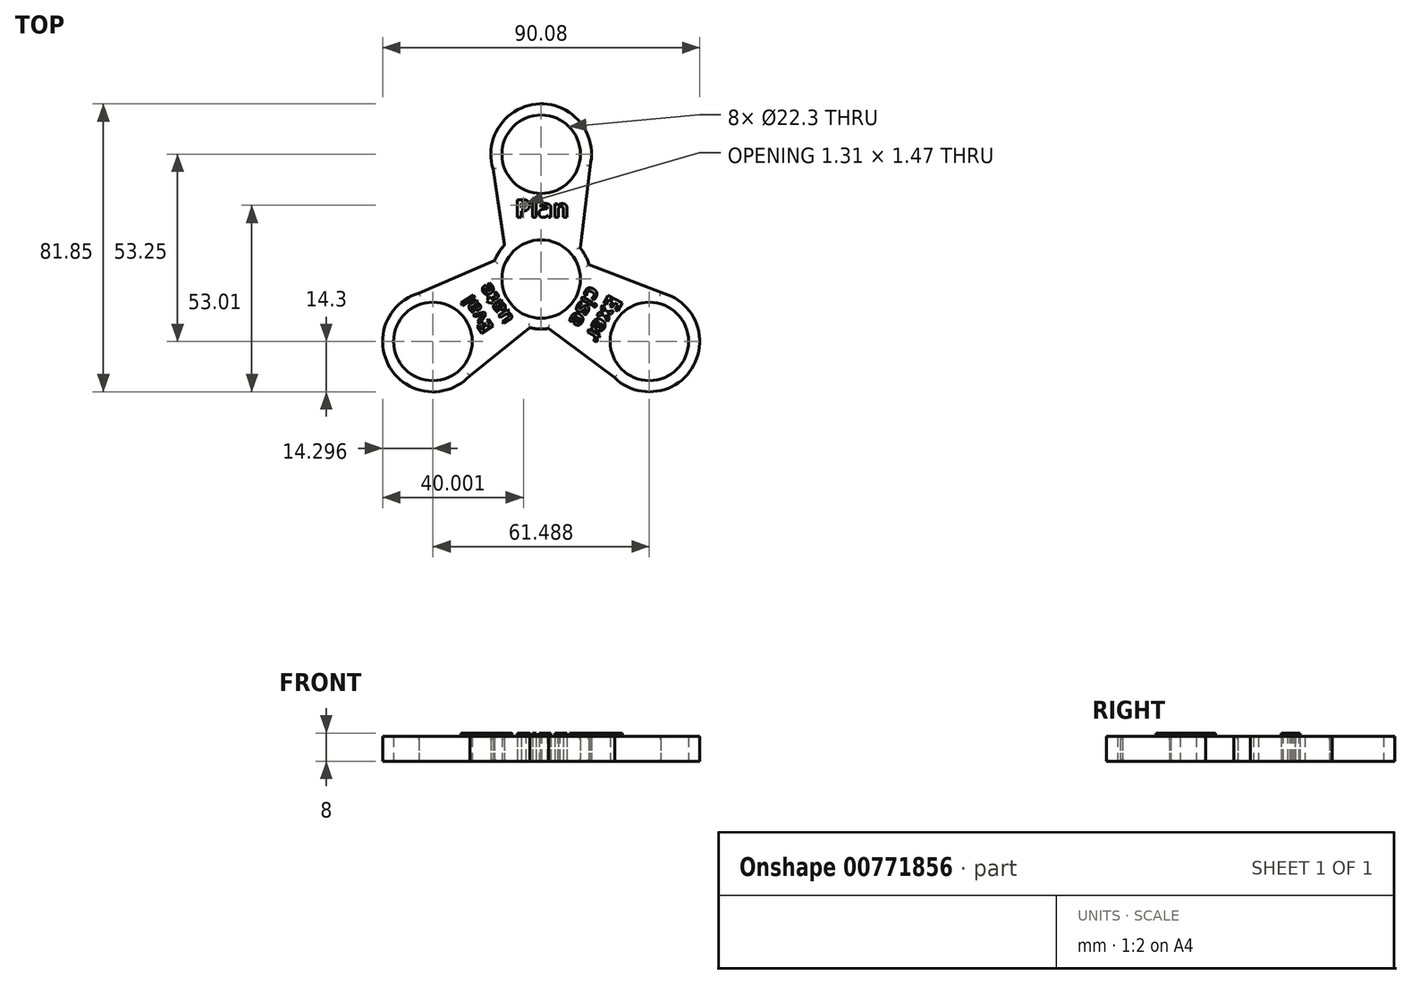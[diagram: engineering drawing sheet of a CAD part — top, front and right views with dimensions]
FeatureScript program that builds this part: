
annotation { "Feature Type Name" : "Feature", "Feature Type Description" : "" }
export const myFeature = defineFeature(function(context is Context, id is Id, definition is map)
    precondition{}
    {
        {
            var Q0;
            Q0=qCreatedBy(makeId("Top.planeOp"),FACE);
            var sketch = newSketch(context, id + "F0", { "sketchPlane" : qUnion([Q0])});
            skCircle(sketch, "E0", {"center": v(0, 0) * mm, "radius": 11.15 * mm});
            skArc(sketch, "E1", {"start": v(-3.17, -13.84) * mm, "mid": v(-0.55, -14.19) * mm, "end": v(2.09, -14.05) * mm});
            skArc(sketch, "E2", {"start": v(13.89, 32.1) * mm, "mid": v(-0.4, 49.8) * mm, "end": v(-13.67, 31.31) * mm});
            skCircle(sketch, "E3", {"center": v(0, 35.5) * mm, "radius": 11.15 * mm});
            skLineSegment(sketch, "E4", {"start": v(13.89, 32.1) * mm, "end": v(11.12, 8.83) * mm});
            skLineSegment(sketch, "E5", {"start": v(-13.67, 31.31) * mm, "end": v(-10.4, 9.66) * mm});
            skArc(sketch, "E6.1.0", {"start": v(-34.74, -4.02) * mm, "mid": v(-42.92, -25.25) * mm, "end": v(-20.28, -27.5) * mm});
            skLineSegment(sketch, "E6.1.1", {"start": v(-20.28, -27.5) * mm, "end": v(-3.17, -13.84) * mm});
            skLineSegment(sketch, "E6.1.2", {"start": v(-34.74, -4.02) * mm, "end": v(-13.2, 5.22) * mm});
            skCircle(sketch, "E6.1.3", {"center": v(-30.74, -17.75) * mm, "radius": 11.15 * mm});
            skArc(sketch, "E6.2.0", {"start": v(20.85, -28.08) * mm, "mid": v(43.33, -24.55) * mm, "end": v(33.95, -3.82) * mm});
            skLineSegment(sketch, "E6.2.1", {"start": v(33.95, -3.82) * mm, "end": v(13.57, 4.18) * mm});
            skLineSegment(sketch, "E6.2.2", {"start": v(20.85, -28.08) * mm, "end": v(2.09, -14.05) * mm});
            skCircle(sketch, "E6.2.3", {"center": v(30.74, -17.75) * mm, "radius": 11.15 * mm});
            skPoint(sketch, "E7.orphan", {"position": v(14.3, 35.55) * mm});
            skPoint(sketch, "E8.orphan", {"position": v(-14.3, 35.46) * mm});
            skPoint(sketch, "E9.orphan", {"position": v(-37.94, -5.4) * mm});
            skPoint(sketch, "E10.orphan", {"position": v(-23.56, -30.12) * mm});
            skArc(sketch, "E11.trimOffspring", {"start": v(13.57, 4.18) * mm, "mid": v(12.56, 6.62) * mm, "end": v(11.12, 8.83) * mm});
            skPoint(sketch, "E12.orphan", {"position": v(23.64, -30.16) * mm});
            skPoint(sketch, "E13.orphan", {"position": v(37.86, -5.35) * mm});
            skArc(sketch, "E14.trimOffspring", {"start": v(-10.4, 9.66) * mm, "mid": v(-12.01, 7.57) * mm, "end": v(-13.2, 5.22) * mm});
            skPoint(sketch, "E15.firstSnap0", {"position": v(-12.04, 20.49) * mm});
            skSolve(sketch);
        }
        {
            var Q0;
            Q0 = qSketchRegion(id + "F0", true);
            extrude(context, id + "F1", {"entities" : qUnion([Q0]), "depth" : 7 * mm, "offsetDistance" : 25 * mm});
        }
        {
            var Q0;
            Q0=makeQuery(id+"F1.opExtrude","CAP_EDGE",EDGE,{"disambiguationData":[OSD([sQuery(id+"F0.wireOp",EDGE,"E2")])],"isStart":false});
            var Q1;
            Q1=makeQuery(id+"F1.opExtrude","CAP_EDGE",EDGE,{"disambiguationData":[OSD([sQuery(id+"F0.wireOp",EDGE,"E2")])],"isStart":true});
            var Q2;
            Q2=makeQuery(id+"F1.opExtrude","SWEPT_EDGE",EDGE,{"disambiguationData":[OSD([sQuery(id+"F0.wireOp",EDGE,"E5"),sQuery(id+"F0.wireOp",EDGE,"E14.trimOffspring")])]});
            var Q3;
            Q3=makeQuery(id+"F1.opExtrude","CAP_EDGE",EDGE,{"disambiguationData":[OSD([sQuery(id+"F0.wireOp",EDGE,"E5")])],"isStart":false});
            var Q4;
            Q4=makeQuery(id+"F1.opExtrude","CAP_EDGE",EDGE,{"disambiguationData":[OSD([sQuery(id+"F0.wireOp",EDGE,"E5")])],"isStart":true});
            var Q5;
            Q5=makeQuery(id+"F1.opExtrude","CAP_EDGE",EDGE,{"disambiguationData":[OSD([sQuery(id+"F0.wireOp",EDGE,"E6.1.2")])],"isStart":true});
            var Q6;
            Q6=makeQuery(id+"F1.opExtrude","CAP_EDGE",EDGE,{"disambiguationData":[OSD([sQuery(id+"F0.wireOp",EDGE,"E14.trimOffspring")])],"isStart":true});
            var Q7;
            Q7=makeQuery(id+"F1.opExtrude","CAP_EDGE",EDGE,{"disambiguationData":[OSD([sQuery(id+"F0.wireOp",EDGE,"E14.trimOffspring")])],"isStart":false});
            var Q8;
            Q8=makeQuery(id+"F1.opExtrude","CAP_EDGE",EDGE,{"disambiguationData":[OSD([sQuery(id+"F0.wireOp",EDGE,"E6.1.2")])],"isStart":false});
            var Q9;
            Q9=makeQuery(id+"F1.opExtrude","CAP_EDGE",EDGE,{"disambiguationData":[OSD([sQuery(id+"F0.wireOp",EDGE,"E6.1.0")])],"isStart":true});
            var Q10;
            Q10=makeQuery(id+"F1.opExtrude","CAP_EDGE",EDGE,{"disambiguationData":[OSD([sQuery(id+"F0.wireOp",EDGE,"E6.1.0")])],"isStart":false});
            var Q11;
            Q11=makeQuery(id+"F1.opExtrude","CAP_EDGE",EDGE,{"disambiguationData":[OSD([sQuery(id+"F0.wireOp",EDGE,"E6.1.1")])],"isStart":true});
            var Q12;
            Q12=makeQuery(id+"F1.opExtrude","CAP_EDGE",EDGE,{"disambiguationData":[OSD([sQuery(id+"F0.wireOp",EDGE,"E6.1.1")])],"isStart":false});
            var Q13;
            Q13=makeQuery(id+"F1.opExtrude","CAP_EDGE",EDGE,{"disambiguationData":[OSD([sQuery(id+"F0.wireOp",EDGE,"E1")])],"isStart":false});
            var Q14;
            Q14=makeQuery(id+"F1.opExtrude","CAP_EDGE",EDGE,{"disambiguationData":[OSD([sQuery(id+"F0.wireOp",EDGE,"E1")])],"isStart":true});
            var Q15;
            Q15=makeQuery(id+"F1.opExtrude","CAP_EDGE",EDGE,{"disambiguationData":[OSD([sQuery(id+"F0.wireOp",EDGE,"E6.2.2")])],"isStart":false});
            var Q16;
            Q16=makeQuery(id+"F1.opExtrude","CAP_EDGE",EDGE,{"disambiguationData":[OSD([sQuery(id+"F0.wireOp",EDGE,"E6.2.2")])],"isStart":true});
            var Q17;
            Q17=makeQuery(id+"F1.opExtrude","CAP_EDGE",EDGE,{"disambiguationData":[OSD([sQuery(id+"F0.wireOp",EDGE,"E6.2.0")])],"isStart":false});
            var Q18;
            Q18=makeQuery(id+"F1.opExtrude","CAP_EDGE",EDGE,{"disambiguationData":[OSD([sQuery(id+"F0.wireOp",EDGE,"E6.2.0")])],"isStart":true});
            var Q19;
            Q19=makeQuery(id+"F1.opExtrude","CAP_EDGE",EDGE,{"disambiguationData":[OSD([sQuery(id+"F0.wireOp",EDGE,"E6.2.1")])],"isStart":false});
            var Q20;
            Q20=makeQuery(id+"F1.opExtrude","CAP_EDGE",EDGE,{"disambiguationData":[OSD([sQuery(id+"F0.wireOp",EDGE,"E6.2.1")])],"isStart":true});
            var Q21;
            Q21=makeQuery(id+"F1.opExtrude","CAP_EDGE",EDGE,{"disambiguationData":[OSD([sQuery(id+"F0.wireOp",EDGE,"E11.trimOffspring")])],"isStart":true});
            var Q22;
            Q22=makeQuery(id+"F1.opExtrude","CAP_EDGE",EDGE,{"disambiguationData":[OSD([sQuery(id+"F0.wireOp",EDGE,"E11.trimOffspring")])],"isStart":false});
            var Q23;
            Q23=makeQuery(id+"F1.opExtrude","CAP_EDGE",EDGE,{"disambiguationData":[OSD([sQuery(id+"F0.wireOp",EDGE,"E4")])],"isStart":false});
            var Q24;
            Q24=makeQuery(id+"F1.opExtrude","CAP_EDGE",EDGE,{"disambiguationData":[OSD([sQuery(id+"F0.wireOp",EDGE,"E4")])],"isStart":true});
            var Q25;
            Q25=makeQuery(id+"F1.opExtrude","CAP_EDGE",EDGE,{"disambiguationData":[OSD([sQuery(id+"F0.wireOp",EDGE,"E6.1.0")])],"isStart":false});
            var Q26;
            Q26=makeQuery(id+"F1.opExtrude","CAP_EDGE",EDGE,{"disambiguationData":[OSD([sQuery(id+"F0.wireOp",EDGE,"E6.2.0")])],"isStart":false});
            var Q27;
            Q27=makeQuery(id+"F1.opExtrude","CAP_EDGE",EDGE,{"disambiguationData":[OSD([sQuery(id+"F0.wireOp",EDGE,"E6.2.0")])],"isStart":true});
            var Q28;
            Q28=makeQuery(id+"F1.opExtrude","CAP_EDGE",EDGE,{"disambiguationData":[OSD([sQuery(id+"F0.wireOp",EDGE,"E6.1.0")])],"isStart":true});
            fillet(context, id + "F2", {"entities" : qUnion([Q0, Q1, Q2, Q3, Q4, Q5, Q6, Q7, Q8, Q9, Q10, Q11, Q12, Q13, Q14, Q15, Q16, Q17, Q18, Q19, Q20, Q21, Q22, Q23, Q24, Q25, Q26, Q27, Q28]), "radius" : 1 * mm, "tangentPropagation" : true, "allowEdgeOverflow" : false});
        }
        {
            var Q0;
            Q0=qCreatedBy(makeId("Top.planeOp"),FACE);
            var sketch = newSketch(context, id + "F3", { "sketchPlane" : qUnion([Q0])});
            skText(sketch, "E16", { "text": "Plan", "fontName": "OpenSans-Bold.ttf"});
            const initialGuessF3  = {"E16": [-0.00737, 0.0176, 1, 0, 0.005]};
            skSetInitialGuess(sketch, initialGuessF3);
            skSolve(sketch);
        }
        {
            var Q0;
            Q0=makeQuery(id+"F3.imprint","IMPRINT",FACE,{"disambiguationData":[TD([[makeQuery(id+"F3.imprint","IMPRINT",EDGE,{"derivedFrom":sQuery(id+"F3.wireOp",EDGE,"E16.sketch_text.stroke-16")}),-1.0]])]});
            var Q1;
            Q1=makeQuery(id+"F3.imprint","IMPRINT",FACE,{"disambiguationData":[TD([[makeQuery(id+"F3.imprint","IMPRINT",EDGE,{"derivedFrom":sQuery(id+"F3.wireOp",EDGE,"E16.sketch_text.stroke-45")}),-1.0]])]});
            var Q2;
            Q2=makeQuery(id+"F3.imprint","IMPRINT",FACE,{"disambiguationData":[TD([[makeQuery(id+"F3.imprint","IMPRINT",EDGE,{"derivedFrom":sQuery(id+"F3.wireOp",EDGE,"E16.sketch_text.stroke-0")}),-1.0]])]});
            var Q3;
            Q3=makeQuery(id+"F3.imprint","IMPRINT",FACE,{"disambiguationData":[TD([[makeQuery(id+"F3.imprint","IMPRINT",EDGE,{"derivedFrom":sQuery(id+"F3.wireOp",EDGE,"E16.sketch_text.stroke-20")}),-1.0]])]});
            var Q4;
            Q4=makeQuery(id+"F3.imprint","IMPRINT",FACE,{"disambiguationData":[TD([[makeQuery(id+"F3.imprint","IMPRINT",EDGE,{"derivedFrom":sQuery(id+"F3.wireOp",EDGE,"E16.sketch_text.stroke-38")}),1.0]])]});
            extrude(context, id + "F4", {"entities" : qUnion([Q0, Q1, Q2, Q3, Q4]), "depth" : 8 * mm, "offsetDistance" : 25 * mm});
        }
        {
            var Q0;
            Q0=qCreatedBy(makeId("Top.planeOp"),FACE);
            var sketch = newSketch(context, id + "F5", { "sketchPlane" : qUnion([Q0])});
            skText(sketch, "E17", { "text": "Eval", "fontName": "OpenSans-Bold.ttf"});
            skText(sketch, "E18", { "text": "uate", "fontName": "OpenSans-Bold.ttf"});
            const initialGuessF5  = {"E17": [-0.01333, -0.01369, -0.54345, 0.83944, 0.004], "E18": [-0.00778, -0.01134, -0.54661, 0.83739, 0.004]};
            skSetInitialGuess(sketch, initialGuessF5);
            skSolve(sketch);
        }
        {
            var Q0;
            Q0 = qSketchRegion(id + "F5", true);
            extrude(context, id + "F6", {"entities" : qUnion([Q0]), "operationType" : NewBodyOperationType.ADD, "depth" : 8 * mm, "offsetDistance" : 25 * mm});
        }
        {
            var Q0;
            Q0=qCreatedBy(makeId("Top.planeOp"),FACE);
            var sketch = newSketch(context, id + "F7", { "sketchPlane" : qUnion([Q0])});
            skText(sketch, "E19", { "text": "Exer", "fontName": "OpenSans-Bold.ttf"});
            skText(sketch, "E20", { "text": "cise", "fontName": "OpenSans-Bold.ttf"});
            const initialGuessF7  = {"E19": [0.01929, -0.00408, -0.48422, -0.87495, 0.00462], "E20": [0.0135, -0.00173, -0.4825, -0.8759, 0.0045]};
            skSetInitialGuess(sketch, initialGuessF7);
            skSolve(sketch);
        }
        {
            var Q0;
            Q0 = qSketchRegion(id + "F7", true);
            extrude(context, id + "F8", {"entities" : qUnion([Q0]), "operationType" : NewBodyOperationType.ADD, "depth" : 8 * mm, "offsetDistance" : 25 * mm});
        }
        {
            var Q0;
            Q0 = qSketchRegion(id + "F7", true);
            extrude(context, id + "F9", {"entities" : qUnion([Q0]), "operationType" : NewBodyOperationType.ADD, "depth" : 8 * mm, "offsetDistance" : 25 * mm});
        }
        {
            var Q0;
            Q0 = qSketchRegion(id + "F0", true);
            extrude(context, id + "F10", {"entities" : qUnion([Q0]), "depth" : 7 * mm, "offsetDistance" : 25 * mm});
        }
    });
